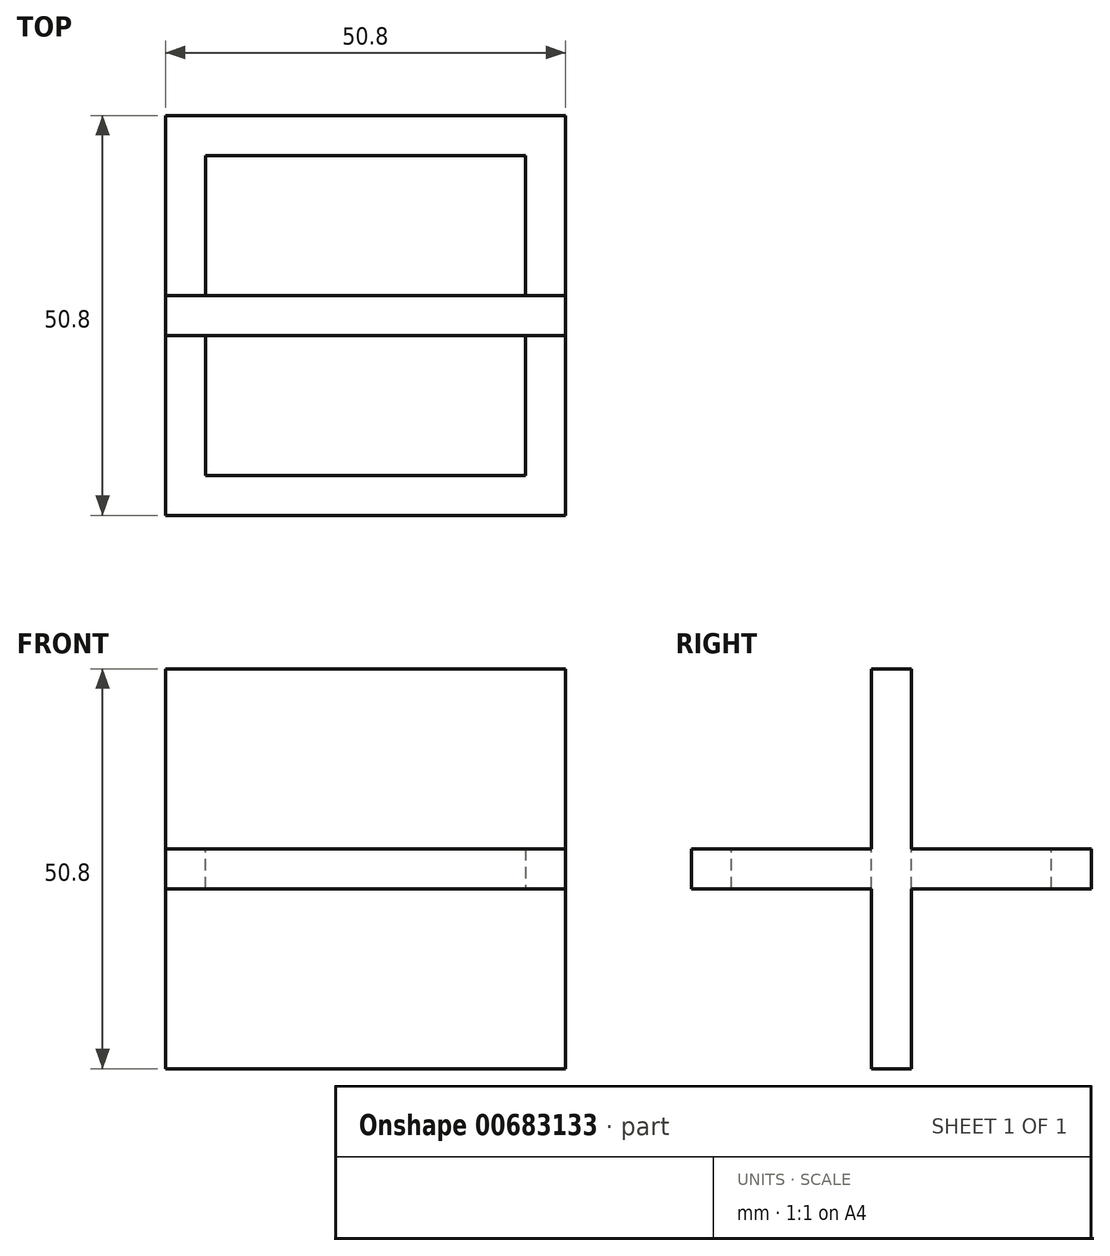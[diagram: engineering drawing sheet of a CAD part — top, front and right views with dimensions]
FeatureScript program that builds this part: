
annotation { "Feature Type Name" : "Feature", "Feature Type Description" : "" }
export const myFeature = defineFeature(function(context is Context, id is Id, definition is map)
    precondition{}
    {
        {
            var Q0;
            Q0=qCreatedBy(makeId("Top.planeOp"),FACE);
            var sketch = newSketch(context, id + "F0", { "sketchPlane" : qUnion([Q0])});
            skLineSegment(sketch, "E0.bottom", {"start": v(-25.4, 25.4) * mm, "end": v(25.4, 25.4) * mm});
            skLineSegment(sketch, "E0.top", {"start": v(-25.4, -25.4) * mm, "end": v(25.4, -25.4) * mm});
            skLineSegment(sketch, "E0.left", {"start": v(-25.4, 25.4) * mm, "end": v(-25.4, -25.4) * mm});
            skLineSegment(sketch, "E0.right", {"start": v(25.4, 25.4) * mm, "end": v(25.4, -25.4) * mm});
            skSolve(sketch);
        }
        {
            var Q0;
            Q0 = qSketchRegion(id + "F0", true);
            extrude(context, id + "F1", {"entities" : qUnion([Q0]), "depth" : 2.54 * mm, "offsetDistance" : 25.4 * mm, "hasSecondDirection" : true, "secondDirectionOppositeDirection" : true, "secondDirectionDepth" : 2.54 * mm});
        }
        {
            var Q0;
            Q0=makeQuery(id+"F1.opExtrude","CAP_FACE",FACE,{"disambiguationData":[OSD([sQuery(id+"F0.wireOp",EDGE,"E0.bottom"),sQuery(id+"F0.wireOp",EDGE,"E0.top"),sQuery(id+"F0.wireOp",EDGE,"E0.left"),sQuery(id+"F0.wireOp",EDGE,"E0.right")])],"isStart":false});
            var sketch = newSketch(context, id + "F2", { "sketchPlane" : qUnion([Q0])});
            skLineSegment(sketch, "E1.0", {"start": v(-20.32, 20.32) * mm, "end": v(-20.32, -20.32) * mm});
            skLineSegment(sketch, "E1.1", {"start": v(20.32, 20.32) * mm, "end": v(-20.32, 20.32) * mm});
            skLineSegment(sketch, "E1.2", {"start": v(20.32, -20.32) * mm, "end": v(20.32, 20.32) * mm});
            skLineSegment(sketch, "E1.3", {"start": v(-20.32, -20.32) * mm, "end": v(20.32, -20.32) * mm});
            skSolve(sketch);
        }
        {
            var Q0;
            Q0 = qSketchRegion(id + "F2", true);
            extrude(context, id + "F3", {"entities" : qUnion([Q0]), "operationType" : NewBodyOperationType.REMOVE, "endBound" : BoundingType.THROUGH_ALL, "oppositeDirection" : true, "depth" : 25.4 * mm, "offsetDistance" : 25.4 * mm});
        }
        {
            var Q0;
            Q0=qCreatedBy(makeId("Front.planeOp"),FACE);
            var sketch = newSketch(context, id + "F4", { "sketchPlane" : qUnion([Q0])});
            skLineSegment(sketch, "E2.bottom", {"start": v(-25.4, 25.4) * mm, "end": v(25.4, 25.4) * mm});
            skLineSegment(sketch, "E2.top", {"start": v(-25.4, -25.4) * mm, "end": v(25.4, -25.4) * mm});
            skLineSegment(sketch, "E2.left", {"start": v(-25.4, 25.4) * mm, "end": v(-25.4, -25.4) * mm});
            skLineSegment(sketch, "E2.right", {"start": v(25.4, 25.4) * mm, "end": v(25.4, -25.4) * mm});
            skSolve(sketch);
        }
        {
            var Q0;
            Q0 = qSketchRegion(id + "F4", true);
            extrude(context, id + "F5", {"entities" : qUnion([Q0]), "operationType" : NewBodyOperationType.ADD, "depth" : 2.54 * mm, "offsetDistance" : 25.4 * mm, "hasSecondDirection" : true, "secondDirectionOppositeDirection" : true, "secondDirectionDepth" : 2.54 * mm});
        }
    });
